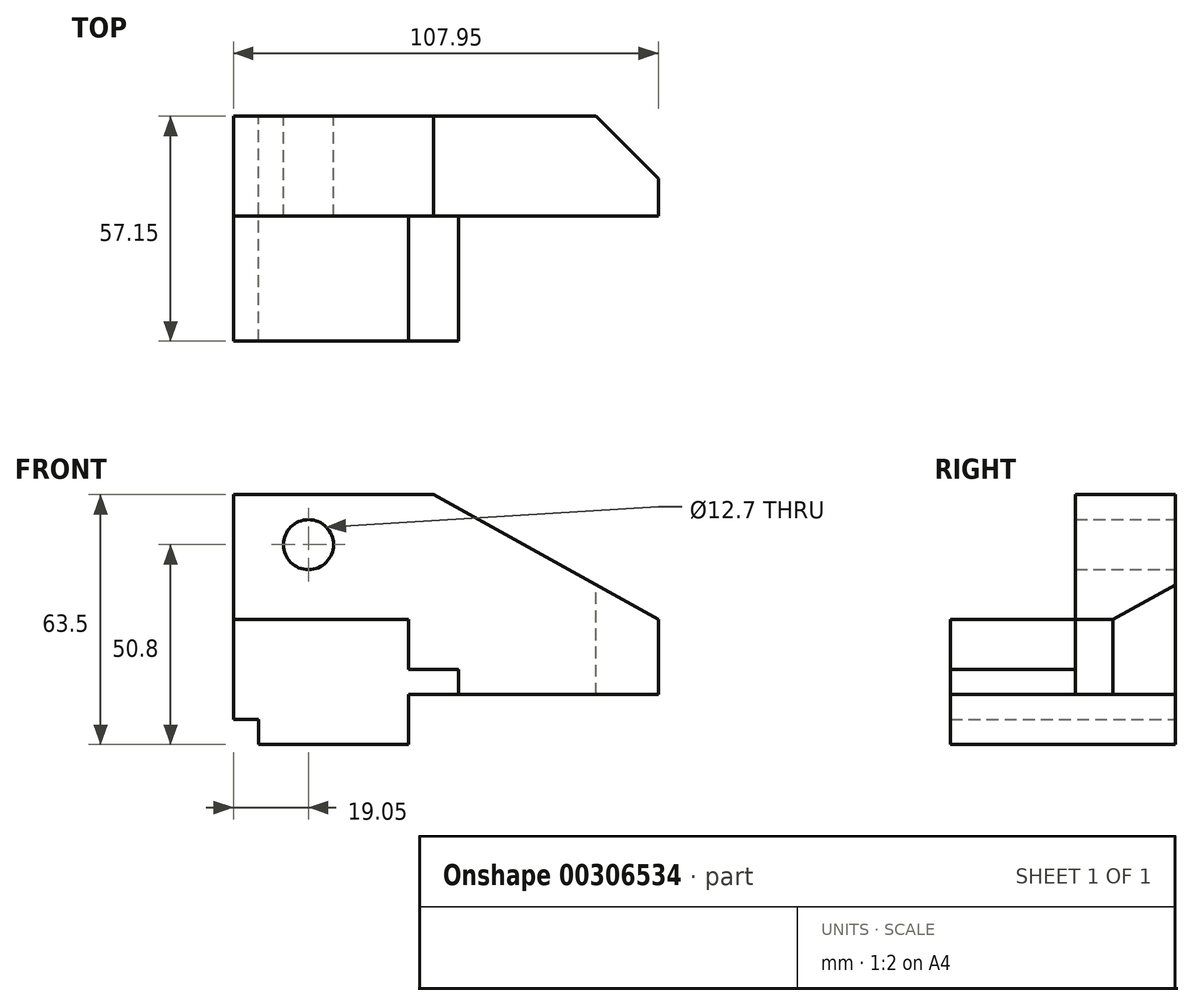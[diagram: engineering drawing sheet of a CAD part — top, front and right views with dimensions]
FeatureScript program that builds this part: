
annotation { "Feature Type Name" : "Feature", "Feature Type Description" : "" }
export const myFeature = defineFeature(function(context is Context, id is Id, definition is map)
    precondition{}
    {
        {
            var Q0;
            Q0=qCreatedBy(makeId("Front.planeOp"),FACE);
            var sketch = newSketch(context, id + "F0", { "sketchPlane" : qUnion([Q0])});
            skLineSegment(sketch, "E0", {"start": v(0, 0) * mm, "end": v(0, 6.35) * mm});
            skLineSegment(sketch, "E1", {"start": v(0, 6.35) * mm, "end": v(-6.35, 6.35) * mm});
            skLineSegment(sketch, "E2", {"start": v(-6.35, 6.35) * mm, "end": v(-6.35, 31.75) * mm});
            skLineSegment(sketch, "E3", {"start": v(-6.35, 31.75) * mm, "end": v(38.1, 31.75) * mm});
            skLineSegment(sketch, "E4", {"start": v(38.1, 31.75) * mm, "end": v(38.1, 19.05) * mm});
            skLineSegment(sketch, "E5", {"start": v(38.1, 19.05) * mm, "end": v(50.8, 19.05) * mm});
            skLineSegment(sketch, "E6", {"start": v(50.8, 19.05) * mm, "end": v(50.8, 12.7) * mm});
            skLineSegment(sketch, "E7", {"start": v(50.8, 12.7) * mm, "end": v(38.1, 12.7) * mm});
            skLineSegment(sketch, "E8", {"start": v(38.1, 12.7) * mm, "end": v(38.1, 0) * mm});
            skLineSegment(sketch, "E9", {"start": v(38.1, 0) * mm, "end": v(0, 0) * mm});
            skLineSegment(sketch, "E10", {"start": v(-6.35, 31.75) * mm, "end": v(-6.35, 63.5) * mm});
            skLineSegment(sketch, "E11", {"start": v(-6.35, 63.5) * mm, "end": v(44.45, 63.5) * mm});
            skLineSegment(sketch, "E12", {"start": v(44.45, 63.5) * mm, "end": v(101.6, 31.75) * mm});
            skLineSegment(sketch, "E13", {"start": v(101.6, 31.75) * mm, "end": v(101.6, 0) * mm});
            skLineSegment(sketch, "E14", {"start": v(101.6, 0) * mm, "end": v(38.1, 0) * mm});
            skCircle(sketch, "E15", {"center": v(12.7, 50.8) * mm, "radius": 6.35 * mm});
            skLineSegment(sketch, "E16", {"start": v(50.8, 12.7) * mm, "end": v(101.6, 12.7) * mm});
            skSolve(sketch);
        }
        {
            var Q0;
            Q0=makeQuery(id+"F0.imprint","IMPRINT",FACE,{"disambiguationData":[TD([[makeQuery(id+"F0.imprint","IMPRINT",EDGE,{"derivedFrom":sQuery(id+"F0.wireOp",EDGE,"E0")}),-1.0]])]});
            extrude(context, id + "F1", {"entities" : qUnion([Q0]), "depth" : 57.15 * mm});
        }
        {
            var Q0;
            Q0=makeQuery(id+"F0.imprint","IMPRINT",FACE,{"disambiguationData":[TD([[makeQuery(id+"F0.imprint","IMPRINT",EDGE,{"derivedFrom":sQuery(id+"F0.wireOp",EDGE,"E3")}),1.0]])]});
            extrude(context, id + "F2", {"entities" : qUnion([Q0]), "operationType" : NewBodyOperationType.ADD, "depth" : 25.4 * mm});
        }
        {
            var Q0;
            Q0=makeQuery(id+"F2.opExtrude","SWEPT_FACE",FACE,{"disambiguationData":[OSD([sQuery(id+"F0.wireOp",EDGE,"E11")])]});
            var sketch = newSketch(context, id + "F3", { "sketchPlane" : qUnion([Q0])});
            skLineSegment(sketch, "E17", {"start": v(44.45, 0) * mm, "end": v(44.45, -25.4) * mm});
            skLineSegment(sketch, "E18", {"start": v(44.45, -25.4) * mm, "end": v(101.6, -25.4) * mm});
            skLineSegment(sketch, "E19", {"start": v(101.6, -25.4) * mm, "end": v(101.6, 0) * mm});
            skLineSegment(sketch, "E20", {"start": v(101.6, 0) * mm, "end": v(44.45, 0) * mm});
            skLineSegment(sketch, "E21", {"start": v(85.72, 0) * mm, "end": v(101.6, -15.88) * mm});
            skSolve(sketch);
        }
        {
            var Q0;
            {var subQ3=sQuery(id+"F3.wireOp",EDGE,"E21");Q0=makeQuery(id+"F3.imprint","IMPRINT",FACE,{"disambiguationData":[TD([[makeQuery(id+"F3.imprint","IMPRINT",EDGE,{"derivedFrom":subQ3}),1.0]])]});}
            extrude(context, id + "F4", {"entities" : qUnion([Q0]), "operationType" : NewBodyOperationType.REMOVE, "endBound" : BoundingType.THROUGH_ALL, "oppositeDirection" : true, "depth" : 25.4 * mm});
        }
    });
